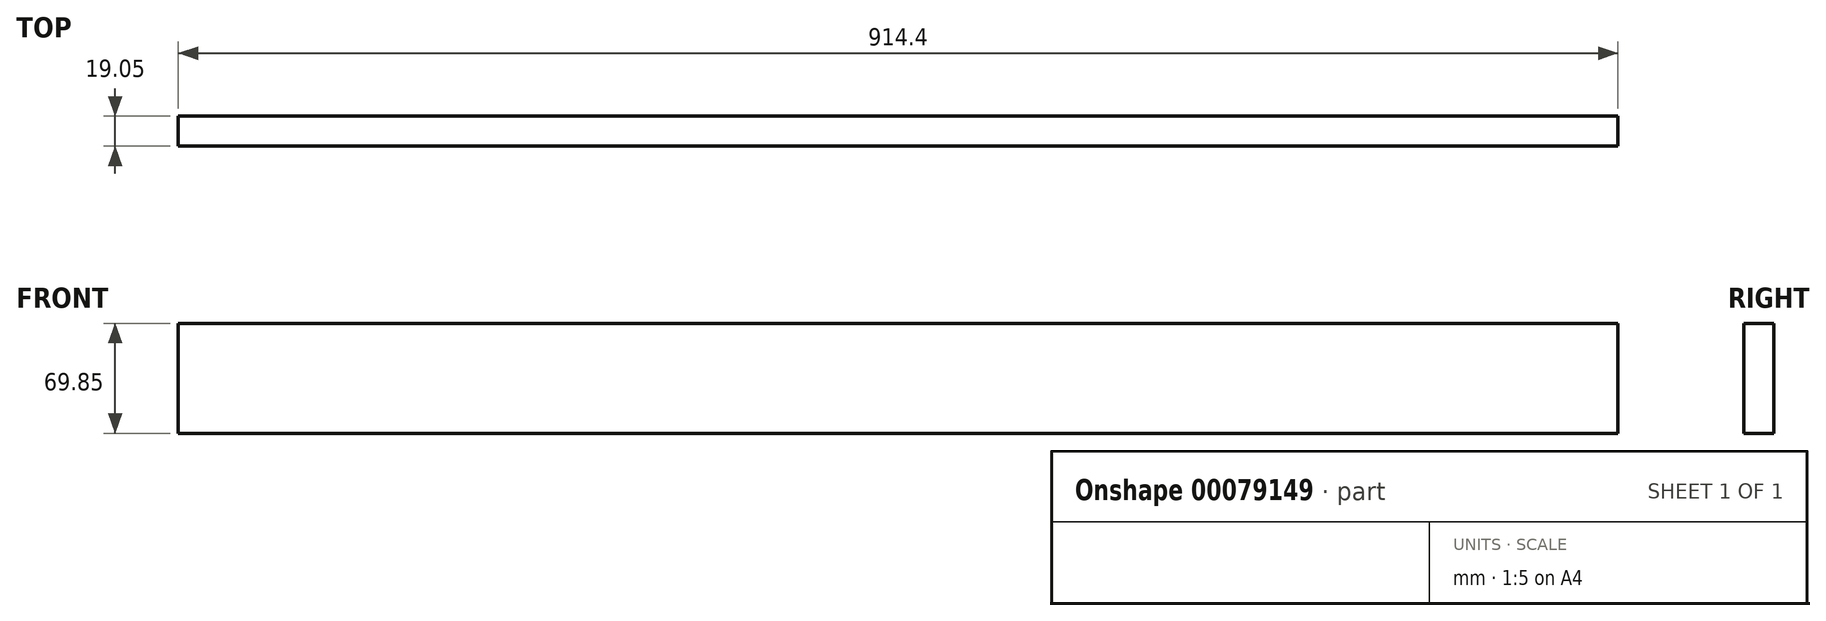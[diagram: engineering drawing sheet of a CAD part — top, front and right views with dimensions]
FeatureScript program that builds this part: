
annotation { "Feature Type Name" : "Feature", "Feature Type Description" : "" }
export const myFeature = defineFeature(function(context is Context, id is Id, definition is map)
    precondition{}
    {
        {
            var Q0;
            Q0=qCreatedBy(makeId("Front.planeOp"),FACE);
            var sketch = newSketch(context, id + "F0", { "sketchPlane" : qUnion([Q0])});
            skLineSegment(sketch, "E0.bottom", {"start": v(752.6, 24.95) * mm, "end": v(-161.8, 24.95) * mm});
            skLineSegment(sketch, "E0.top", {"start": v(752.6, -44.9) * mm, "end": v(-161.8, -44.9) * mm});
            skLineSegment(sketch, "E0.left", {"start": v(752.6, 24.95) * mm, "end": v(752.6, -44.9) * mm});
            skLineSegment(sketch, "E0.right", {"start": v(-161.8, 24.95) * mm, "end": v(-161.8, -44.9) * mm});
            skSolve(sketch);
        }
        {
            var Q0;
            Q0=makeQuery(id+"F0.imprint","IMPRINT",FACE,{"disambiguationData":[TD([[makeQuery(id+"F0.imprint","IMPRINT",EDGE,{"derivedFrom":sQuery(id+"F0.wireOp",EDGE,"E0.bottom")}),1.0]])]});
            extrude(context, id + "F1", {"entities" : qUnion([Q0]), "depth" : 19.05 * mm});
        }
    });
